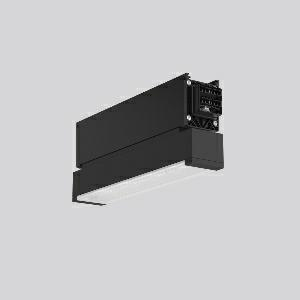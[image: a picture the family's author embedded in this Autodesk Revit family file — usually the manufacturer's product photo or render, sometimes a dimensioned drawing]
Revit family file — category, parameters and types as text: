
# Revit family: linedo_module_rw_9503rw_763_434_00c_0957
name_source: partatom
category: Lighting Fixtures
units: mm (PartAtom-declared; Revit-internal decimal feet)

## family parameters
Cut with Voids When Loaded = No
Host = Face
Light Source = No
Part Type = Normal
Room Calculation Point = No
Round Connector Dimension = Use Diameter
Shared = No

## types (1)
- LINEDO Module RW (1 x LED Modul 763, 390 lm, 6300)
    Apparent Load = 6 VA
    CIE Flux Codes = 36 68 94 98 100
    Color Rendering = 70
    Color Temperature = 6300
    Default Elevation = 1800 mm
    Description = LINEDO, 6 W, 390 lm, 763, black, on/off
Continuous line luminaire, L 342 B 58 H 131, SBS, 3 h, emergency-180 lm, MultiDigit
    Height = 131 mm
    Lamp = 1 x LED Modul 763
    Lamp Light Flux = 390 lm
    Lamp count = 1
    Length = 342 mm
    Lifetime = 50000 h
    Luminous efficacy = 65 lm/W
    Manufacturer = RZB
    ModVariant = No
    Model = 9503RW.763.434.00C
    Mounting Place = Ceiling
    Mounting Type = Surface mounted
    Number of Poles = 1
    OnlyDefault = Yes
    Power Factor = 1
    Product Name = LINEDO Module RW
    Product group = Continuous line luminaire system Linedo IP 54
    ProductGroupID = 314
    Protection Class = Protection class I
    Protection Degree = IP 54
    RLX_Detail_Level = 1
    RLX_Emergency_Light_Flux = 180 lm
    RLX_Emergency_Type = 3
    RLX_Emergency_Type_DB = Yes
    RlxData = <blob elided: 34925 chars, md5=17cca218>
    Socket = socket
    Standby Power = 0 W
    System Light Flux = 390 lm
    System Power = 6 W
    Type Comments = Product without accessories
    Type Image = 9503rf.763.430.00c.jpg
    URL = http://relux.com
    VarID = ---
    Voltage = 230 V
    Voltage Range = 220-240 V
    Weight = 0.00 kg
    Width = 58 mm

## geometry (parser evidence)
native form markers: Blend x4, Sweep x9
no freeform markers — native parametric forms only
